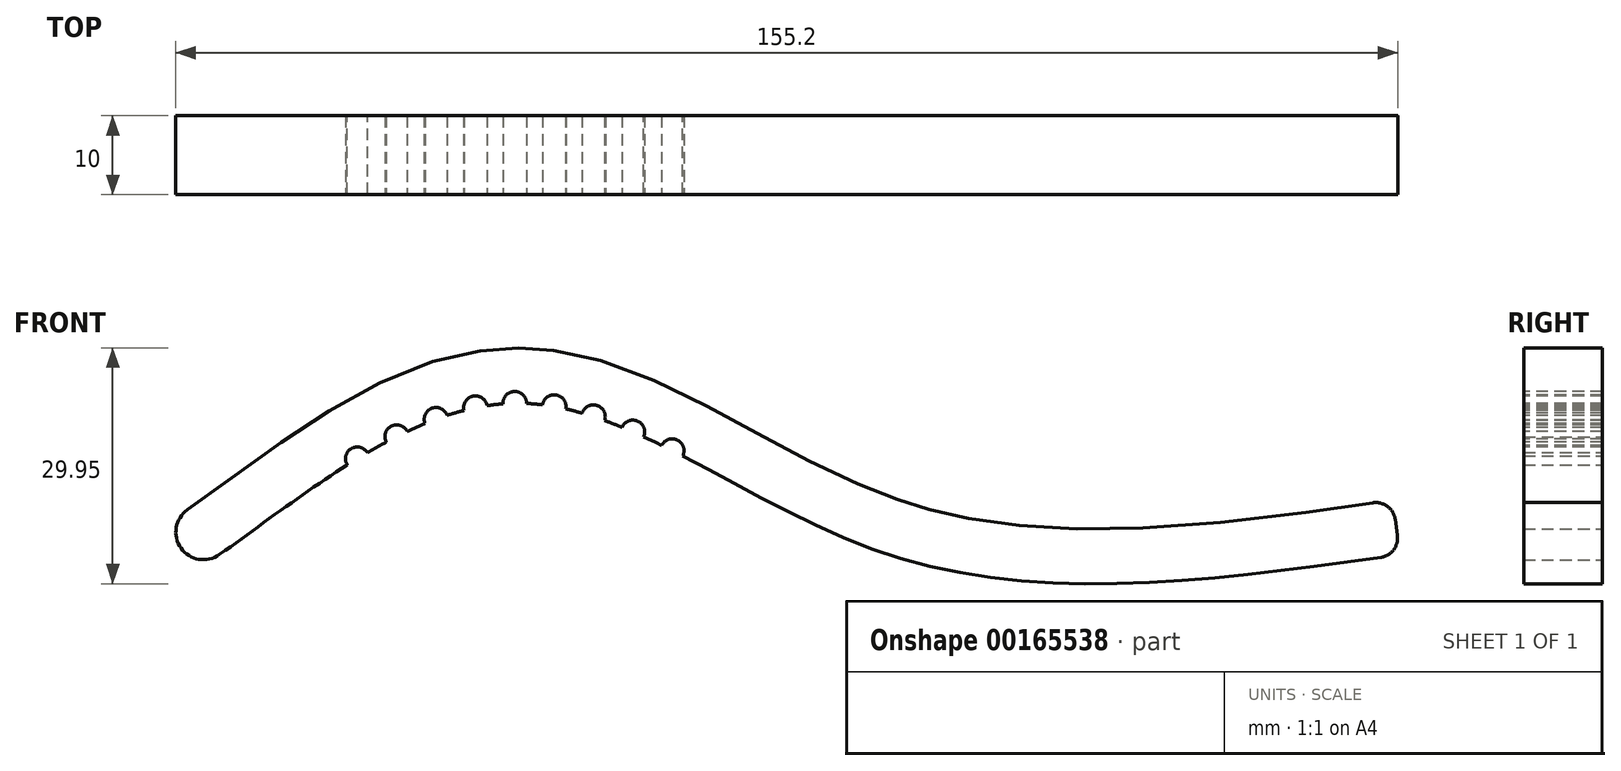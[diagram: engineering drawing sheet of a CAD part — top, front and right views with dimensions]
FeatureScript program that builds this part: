
annotation { "Feature Type Name" : "Feature", "Feature Type Description" : "" }
export const myFeature = defineFeature(function(context is Context, id is Id, definition is map)
    precondition{}
    {
        {
            var Q0;
            Q0=qCreatedBy(makeId("Front.planeOp"),FACE);
            var sketch = newSketch(context, id + "F0", { "sketchPlane" : qUnion([Q0])});
            skFitSpline(sketch, "E0", {"points": [v(0, 0) * mm, v(38.6, 19.22) * mm, v(85, 0) * mm, v(150, 0) * mm], "startDerivative": vector(125.86, 89.11) * mm, "endDerivative": vector(182.2, 25.52) * mm});
            skFitSpline(sketch, "E1.0", {"points": [v(-4.04, 5.71) * mm, v(-1.49, 7.52) * mm, v(2.43, 10.4) * mm, v(7.83, 14.23) * mm, v(11.99, 17) * mm, v(16.26, 19.61) * mm, v(20.7, 21.96) * mm, v(25.3, 23.93) * mm, v(29.34, 25.16) * mm, v(32.68, 25.83) * mm, v(35.24, 26.15) * mm, v(37.42, 26.25) * mm, v(39.19, 26.21) * mm, v(40.94, 26.1) * mm, v(43.1, 25.84) * mm, v(46.47, 25.18) * mm, v(50.55, 23.97) * mm, v(55.28, 22.08) * mm, v(59.88, 19.9) * mm, v(64.4, 17.54) * mm, v(68.9, 15.11) * mm, v(73.35, 12.73) * mm, v(77.8, 10.47) * mm, v(81.5, 8.8) * mm, v(84.44, 7.6) * mm, v(86.28, 6.94) * mm, v(87.75, 6.46) * mm, v(89.24, 6.01) * mm, v(91.12, 5.5) * mm, v(93.42, 4.97) * mm, v(96.54, 4.37) * mm, v(100.54, 3.8) * mm, v(105.5, 3.4) * mm, v(110.6, 3.27) * mm, v(117.56, 3.38) * mm, v(126.55, 4.02) * mm, v(137.67, 5.34) * mm, v(145.23, 6.4) * mm, v(149.03, 6.93) * mm]});
            skLineSegment(sketch, "E2", {"start": v(149.03, 6.93) * mm, "end": v(150, 0) * mm});
            skArc(sketch, "E3", {"start": v(-4.04, 5.71) * mm, "mid": v(-4.88, 0.83) * mm, "end": v(0, 0) * mm});
            skSolve(sketch);
        }
        {
            var Q0;
            Q0 = qSketchRegion(id + "F0", true);
            extrude(context, id + "F1", {"entities" : qUnion([Q0]), "endBound" : BoundingType.SYMMETRIC, "depth" : 10 * mm});
        }
        {
            var Q0;
            Q0=makeQuery(id+"F1.opExtrude","SWEPT_EDGE",EDGE,{"disambiguationData":[OSD([sQuery(id+"F0.wireOp",EDGE,"E1.0"),sQuery(id+"F0.wireOp",EDGE,"6Faxudxn-1uMk-8ccC-NPzW-HdiGVZOxfaOw")])]});
            var Q1;
            Q1=makeQuery(id+"F1.opExtrude","SWEPT_EDGE",EDGE,{"disambiguationData":[OSD([sQuery(id+"F0.wireOp",EDGE,"E0"),sQuery(id+"F0.wireOp",EDGE,"6Faxudxn-1uMk-8ccC-NPzW-HdiGVZOxfaOw")])]});
            fillet(context, id + "F2", {"entities" : qUnion([Q0, Q1]), "radius" : 2.5 * mm, "tangentPropagation" : true, "allowEdgeOverflow" : false});
        }
        {
            var Q0;
            Q0=makeQuery(id+"F1.opExtrude","CAP_FACE",FACE,{"disambiguationData":[OSD([sQuery(id+"F0.wireOp",EDGE,"E0"),sQuery(id+"F0.wireOp",EDGE,"E1.0"),sQuery(id+"F0.wireOp",EDGE,"E2"),sQuery(id+"F0.wireOp",EDGE,"E3")])],"isStart":false});
            var sketch = newSketch(context, id + "F3", { "sketchPlane" : qUnion([Q0])});
            skCircle(sketch, "E4", {"center": v(37.53, 19.22) * mm, "radius": 1.5 * mm});
            skCircle(sketch, "E5", {"center": v(32.53, 18.65) * mm, "radius": 1.5 * mm});
            skCircle(sketch, "E6", {"center": v(27.53, 17.2) * mm, "radius": 1.5 * mm});
            skCircle(sketch, "E7", {"center": v(22.53, 14.98) * mm, "radius": 1.5 * mm});
            skCircle(sketch, "E8", {"center": v(17.53, 12.18) * mm, "radius": 1.5 * mm});
            skCircle(sketch, "E9", {"center": v(42.53, 18.8) * mm, "radius": 1.5 * mm});
            skCircle(sketch, "E10", {"center": v(47.53, 17.52) * mm, "radius": 1.5 * mm});
            skCircle(sketch, "E11", {"center": v(52.53, 15.58) * mm, "radius": 1.5 * mm});
            skCircle(sketch, "E12", {"center": v(57.53, 13.21) * mm, "radius": 1.5 * mm});
            skSolve(sketch);
        }
        {
            var Q0;
            Q0 = qSketchRegion(id + "F3", true);
            extrude(context, id + "F4", {"entities" : qUnion([Q0]), "operationType" : NewBodyOperationType.REMOVE, "endBound" : BoundingType.THROUGH_ALL, "oppositeDirection" : true, "depth" : 25 * mm});
        }
    });
